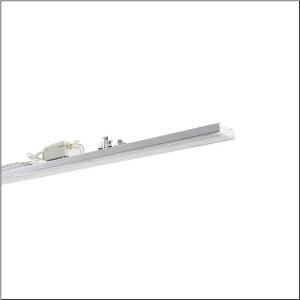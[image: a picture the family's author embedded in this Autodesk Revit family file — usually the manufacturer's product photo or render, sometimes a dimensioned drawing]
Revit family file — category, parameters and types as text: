
# Revit family: licross_r__21_recessed_ho_52te12dn4fxm3s4_e70e
name_source: partatom
category: Lighting Fixtures
units: mm (PartAtom-declared; Revit-internal decimal feet)

## family parameters
Cut with Voids When Loaded = No
Host = Face
Light Source = No
Part Type = Normal
Room Calculation Point = No
Round Connector Dimension = Use Diameter
Shared = No

## types (1)
- --- (1 x LED, 930 lm, 7.5 W, 4000K)
    Apparent Load = 8 VA
    CIE Flux Codes = 69 91 98 100 100
    Color Rendering = 80
    Color Temperature = 4000K
    Default Elevation = 1800 mm
    Description = Licross® 21 Recessed HO, luminaire insert, of sheet steel, galvanised, coil coated, white, length: 1.500mm, width: 66mm, height: 67mm, LED rated luminous flux: 15.000lm, light colour: 840, control gear: DALI 2, with plug, 6-pole, with phase selection, for trunking rail, 9 or 11-core, mains connection: 220..240V, AC, 50/60Hz, rated input power: 88W, halogen-free wiring, for emergency light function, for trunking rail, 9-/11-core, converter,control gear: single battery element, battery: LiFeP04, 9Ah, primary optical cover: cover, of PMMA, light emission: direct distribution, primary light characteristic: symmetric, protection rating (complete): IP54, insulation class (complete): insulation class I (protective earthing), certification: CE, UKCA, protection symbol: D if used in an environment with non-conductive dust loads with corresponding accessories, impact resistance: IK06, permissible ambient temperature for indoor applications: +5..+30°C, standard: EN 60598-2-22, LABS conformity tested according to VDMA 24364:2018-05, reducing of maximum allowable ambient temperature of 5°C with ceiling mounting, corresponds to IFS (International Featured Standards) requirements for safety and quality in the food industry, packaging unit: 1 piece
    Height = 58 mm
    Lamp = 1 x LED
    Lamp Light Flux = 930 lm
    Lamp Power = 7.5 W
    Lamp count = 1
    Length = 1500 mm
    Luminous efficacy = 124 lm/W
    Manufacturer = Siteco
    ModVariant = No
    Model = 52TE12DN4FXM3S4
    Mounting Place = Ceiling
    Mounting Type = Pendant
    Number of Poles = 1
    OnlyDefault = Yes
    Power Factor = 1
    Product Name = Licross® 21 Recessed HO
    Product group = luminaire insert
    ProductGroupID = 901
    Protection Class = Protection class I
    Protection Degree = IP 54
    RLX_Detail_Level = 1
    RLX_Emergency_Light_Flux = 0 lm
    RLX_Emergency_Type = 0
    RLX_Emergency_Type_DB = No
    RlxData = <blob elided: 25101 chars, md5=0db6243e>
    Socket = socket
    Standby Power = 0 W
    System Light Flux = 930 lm
    System Power = 8 W
    Type Comments = : emergency light operation: 3 h
    Type Image = l_1296930.jpg
    URL = http://relux.com
    VarID = @adj_039441
    Voltage = 0 V
    Weight = 0.00 kg
    Width = 66 mm

## geometry (parser evidence)
native form markers: Blend x4, Sweep x13
no freeform markers — native parametric forms only
